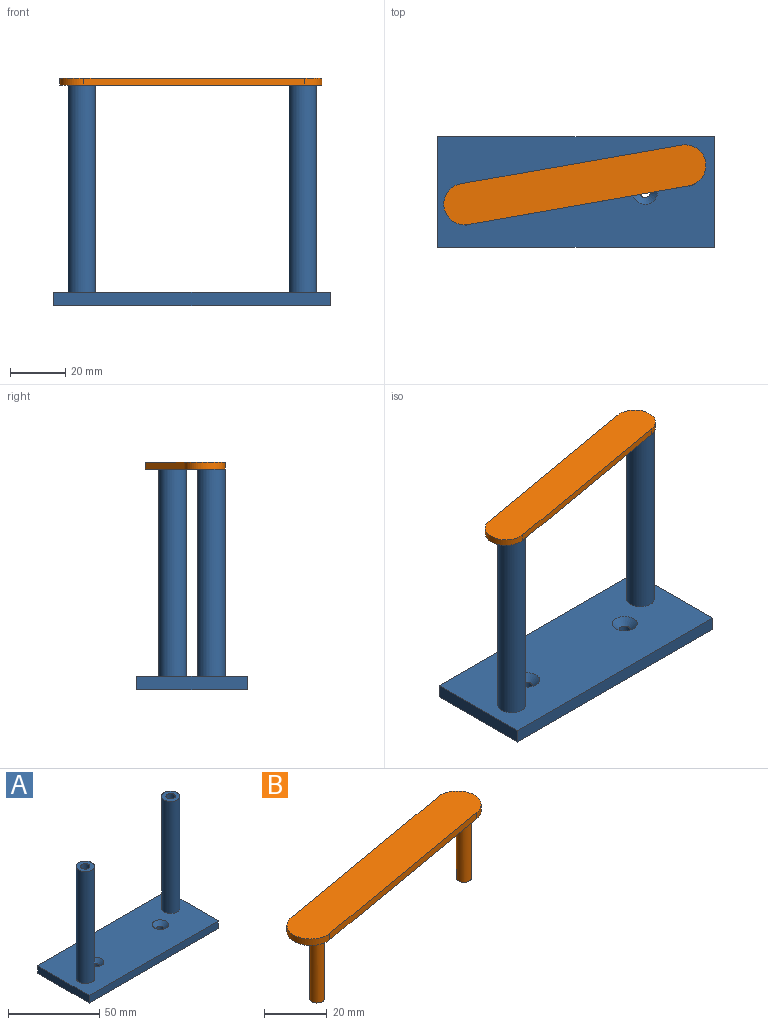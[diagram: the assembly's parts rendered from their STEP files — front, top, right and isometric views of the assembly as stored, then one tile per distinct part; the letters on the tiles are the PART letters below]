
ASSEMBLY  parts=2 mates=1
PART A: 18 faces, bbox 100x40x80 mm
  f0: plane 40x5mm, normal (1,0,0), area 200mm2, adj f1,f3,f4,f5
  f1: plane 100x5mm, normal (0,1,0), area 500mm2, adj f0,f2,f4,f5
  f2: plane 40x5mm, normal (-1,0,0), area 200mm2, adj f1,f3,f4,f5
  f3: plane 100x5mm, normal (0,-1,0), area 500mm2, adj f0,f2,f4,f5
  f4: plane 100x40mm, normal (0,0,-1), area 3974.9mm2, adj f0,f1,f2,f3,f6,f8
  f5: plane 100x40mm, normal (0,0,1), area 3715.7mm2, adj f0,f1,f2,f3,f7,f9,f10,f14
  f6: cylinder r=2mm len=4mm, axis (0,0,1), area 31.4mm2, adj f4,f7
  f7: cone r=2mm half-angle=45deg, axis (0,0,1), area 72.2mm2, adj f5,f6
  f8: cylinder r=2mm len=4mm, axis (0,0,1), area 31.4mm2, adj f4,f9
  f9: cone r=2mm half-angle=45deg, axis (0,0,1), area 72.2mm2, adj f5,f8
  f10: cylinder r=5mm len=75mm, axis (0,0,-1), area 2356.2mm2, adj f5,f11
  f11: plane 10x10mm, normal (0,0,1), area 58.1mm2, adj f10,f12
  f12: cylinder r=2.55mm len=27mm, axis (0,0,1), area 432.6mm2, adj f11,f13
  f13: plane 5.1x5.1mm, normal (0,0,1), area 20.4mm2, adj f12
  f14: cylinder r=5mm len=75mm, axis (0,0,-1), area 2356.2mm2, adj f5,f15
  f15: plane 10x10mm, normal (0,0,1), area 58.1mm2, adj f14,f16
  f16: cylinder r=2.55mm len=27mm, axis (0,0,1), area 432.6mm2, adj f15,f17
  f17: plane 5.1x5.1mm, normal (0,0,1), area 20.4mm2, adj f16
PART B: 10 faces, bbox 95x29x27.5 mm
  f0: plane 4.75x4.75mm, normal (0,0,-1), area 17.7mm2, adj f1
  f1: cylinder r=2.38mm len=25mm, axis (0,0,-1), area 373.1mm2, adj f0,f7
  f2: plane 80x14mm, normal (-0.17,0.99,0), area 203mm2, adj f3,f5,f6,f7
  f3: cylinder r=7.5mm len=14.89mm, axis (0,0,-1), area 58.9mm2, adj f2,f4,f6,f7
  f4: plane 80x14mm, normal (0.17,-0.99,0), area 203mm2, adj f3,f5,f6,f7
  f5: cylinder r=7.5mm len=14.89mm, axis (0,0,-1), area 58.9mm2, adj f2,f4,f6,f7
  f6: plane 95x29mm, normal (0,0,1), area 1395mm2, adj f2,f3,f4,f5
  f7: plane 95x29mm, normal (0,0,-1), area 1359.5mm2, adj f1,f2,f3,f4,f5,f9
  f8: plane 4.75x4.75mm, normal (0,0,-1), area 17.7mm2, adj f9
  f9: cylinder r=2.38mm len=25mm, axis (0,0,-1), area 373.1mm2, adj f7,f8
PLACE A at identity
PLACE B at identity
MATE fastened B.f9 <-> A.f14  axis (0,0,-1) through (-40,-7,75)mm
